# Revit family: MECON Turbo-Lux® 3 Digital
name_source: partatom
category: Rohrzubehör
units: mm (PartAtom-declared; Revit-internal decimal feet)

## family parameters
Arbeitsebenenbasiert = Nein
Beim Laden mit Abzugskörper schneiden = Nein
Bemaßung runder Anschluss = Radius verwenden
Gemeinsam genutzt = Nein
Immer vertikal = Ja
OmniClass-Nummer = 23.60.10.17
OmniClass-Titel = Flow Meters
Teiletyp = Ventil - Zerlegung in

## types (57) — shared parameters
Approval = FM
Black = Metal - black
Blue = Metal - RAL5015
Delivery Time = in stock
Download Test Certificate = https://download.mecon.de
FM Certificate = https://www.mecon.de
Glass = Glass-
Grey = Metal - grey
Hersteller = MECON GmbH, Röntgenstraße 105, 50169 Kerpen, Germany
IfcExportAs = IfcFlowMeter
IfcExportType = FLOWMETER
Operating Manual = https://www.mecon.de
Technical Data Sheet = https://www.mecon.de
URL = https://www.mecon.de
Website Product = https://www.mecon.de
iFM = Ja
iLPCB = Nein
iVdS = Nein
zero-valued in all types: Vorgabe-Ansicht

## per-type parameters (varying)
| type | Build in Length | Color_Body | Flow Range | Modell | Nominal_Diameter | Nominal_Radius | Order Code | Typenkommentare | iD2 | iR1 |
| 12"/ DN 300, 5000 USgpm (ø 323,9 mm) - stainless steel | 200 mm  [stored 0.656168 ft] | Metal - stainless steel | 2000 - 10000 USgpm / 7600 - 38000 lpm | 12"/ DN 300 for pump 5000 USgpm (ø 323,9 mm) with FM approval | 300 mm | 150 mm | TL3P0-NWS / TL3D0 | 12"/ DN 300, 5000 USgpm (ø 323,9 mm) FM - stainless steel | 240 mm  [stored 0.787402 ft] | 154 mm  [stored 0.505249 ft] |
| 12"/ DN 300, 5000 USgpm (ø 323,9 mm) - red | 200 mm  [stored 0.656168 ft] | Metal - RAL3000 | 2000 - 10000 USgpm / 7600 - 38000 lpm | 12"/ DN 300 for pump 5000 USgpm (ø 323,9 mm) with FM approval | 300 mm | 150 mm | TL3P0-NWR / TL3D0 | 12"/ DN 300, 5000 USgpm (ø 323,9 mm) FM - red | 240 mm  [stored 0.787402 ft] | 154 mm  [stored 0.505249 ft] |
| 12"/ DN 300, 5000 USgpm (ø 323,9 mm) | 200 mm  [stored 0.656168 ft] | Metal - RAL5015 | 2000 - 10000 USgpm / 7600 - 38000 lpm | 12"/ DN 300 for pump 5000 USgpm (ø 323,9 mm) with FM approval | 300 mm | 150 mm | TL3P0-NW / TL3D0 | 12"/ DN 300, 5000 USgpm (ø 323,9 mm)  FM | 240 mm  [stored 0.787402 ft] | 154 mm  [stored 0.505249 ft] |
| 10"/ DN 250, 4500 USgpm (ø 273,0 mm) - stainless steel | 200 mm  [stored 0.656168 ft] | Metal - stainless steel | 1800 - 9000 USgpm / 6800 - 34000 lpm | 10"/ DN 250 for pump 4500 USgpm (ø 273,0 mm) with FM approval | 250 mm | 125 mm | TL3P0-MVS / TL3D0 | 10"/ DN 250, 4500 USgpm (ø 273,0 mm) FM - stainless steel | 215 mm  [stored 0.705381 ft] | 129 mm |
| 10"/ DN 250, 4500 USgpm (ø 273,0 mm) - red | 200 mm  [stored 0.656168 ft] | Metal - RAL3000 | 1800 - 9000 USgpm / 6800 - 34000 lpm | 10"/ DN 250 for pump 4500 USgpm (ø 273,0 mm) with FM approval | 250 mm | 125 mm | TL3P0-MVR / TL3D0 | 10"/ DN 250, 4500 USgpm (ø 273,0 mm) FM - red | 215 mm  [stored 0.705381 ft] | 129 mm |
| 10"/ DN 250, 4500 USgpm (ø 273,0 mm) | 200 mm  [stored 0.656168 ft] | Metal - RAL5015 | 1800 - 9000 USgpm / 6800 - 34000 lpm | 10"/ DN 250 for pump 4500 USgpm (ø 273,0 mm) with FM approval | 250 mm | 125 mm | TL3P0-MV / TL3D0 | 10"/ DN 250, 4500 USgpm (ø 273,0 mm)  FM | 215 mm  [stored 0.705381 ft] | 129 mm |
| 10"/ DN 250, 4000 USgpm (ø 273,0 mm) - stainless steel | 200 mm  [stored 0.656168 ft] | Metal - stainless steel | 1600 - 8000 USgpm / 6000 - 30000 lpm | 10"/ DN 250 for pump 4000 USgpm (ø 273,0 mm) with FM approval | 250 mm | 125 mm | TL3P0-MUS / TL3D0 | 10"/ DN 250, 4000 USgpm (ø 273,0 mm) FM - stainless steel | 215 mm  [stored 0.705381 ft] | 129 mm |
| 10"/ DN 250, 4000 USgpm (ø 273,0 mm) - red | 200 mm  [stored 0.656168 ft] | Metal - RAL3000 | 1600 - 8000 USgpm / 6000 - 30000 lpm | 10"/ DN 250 for pump 4000 USgpm (ø 273,0 mm) with FM approval | 250 mm | 125 mm | TL3P0-MUR / TL3D0 | 10"/ DN 250, 4000 USgpm (ø 273,0 mm) FM - red | 215 mm  [stored 0.705381 ft] | 129 mm |
| 10"/ DN 250, 4000 USgpm (ø 273,0 mm) | 200 mm  [stored 0.656168 ft] | Metal - RAL5015 | 1600 - 8000 USgpm / 6000 - 30000 lpm | 10"/ DN 250 for pump 4000 USgpm (ø 273,0 mm) with FM approval | 250 mm | 125 mm | TL3P0-MU / TL3D0 | 10"/ DN 250, 4000 USgpm (ø 273,0 mm)  FM | 215 mm  [stored 0.705381 ft] | 129 mm |
| 10"/ DN 250, 3500 USgpm (ø 273,0 mm) - stainless steel | 200 mm  [stored 0.656168 ft] | Metal - stainless steel | 1400 - 7000 USgpm / 5300 - 26500 lpm | 10"/ DN 250 for pump 3500 USgpm (ø 273,0 mm) with FM approval | 250 mm | 125 mm | TL3P0-MTS / TL3D0 | 10"/ DN 250, 3500 USgpm (ø 273,0 mm) - stainless steel | 215 mm  [stored 0.705381 ft] | 129 mm |
| 10"/ DN 250, 3500 USgpm (ø 273,0 mm) - red | 200 mm  [stored 0.656168 ft] | Metal - RAL3000 | 1400 - 7000 USgpm / 5300 - 26500 lpm | 10"/ DN 250 for pump 3500 USgpm (ø 273,0 mm) with FM approval | 250 mm | 125 mm | TL3P0-MTR / TL3D0 | 10"/ DN 250, 3500 USgpm (ø 273,0 mm) FM - red | 215 mm  [stored 0.705381 ft] | 129 mm |
| 10"/ DN 250, 3500 USgpm (ø 273,0 mm) | 200 mm  [stored 0.656168 ft] | Metal - RAL5015 | 1400 - 7000 USgpm / 5300 - 26500 lpm | 10"/ DN 250 for pump 3500 USgpm (ø 273,0 mm) with FM approval | 250 mm | 125 mm | TL3P0-MT / TL3D0 | 10"/ DN 250, 3500 USgpm (ø 273,0 mm) FM | 215 mm  [stored 0.705381 ft] | 129 mm |
| 8"/ DN 200, 3000 USgpm (ø 219,1 mm) - stainless steel | 200 mm  [stored 0.656168 ft] | Metal - stainless steel | 1200 - 6000 USgpm / 4500 - 22500 lpm | 8"/ DN 200 for pump 3000 USgpm (ø 219,1 mm) with FM approval | 200 mm | 100 mm | TL3P0-LSS / TL3D0 | 8"/ DN 200, 3000 USgpm (ø 219,1 mm) FM - stainless steel | 190 mm  [stored 0.62336 ft] | 104 mm |
| 8"/ DN 200, 3000 USgpm (ø 219,1 mm) - red | 200 mm  [stored 0.656168 ft] | Metal - RAL3000 | 1200 - 6000 USgpm / 4500 - 22500 lpm | 8"/ DN 200 for pump 3000 USgpm (ø 219,1 mm) with FM approval | 200 mm | 100 mm | TL3P0-LSR / TL3D0 | 8"/ DN 200, 3000 USgpm (ø 219,1 mm) FM - red | 190 mm  [stored 0.62336 ft] | 104 mm |
| 8"/ DN 200, 3000 USgpm (ø 219,1 mm) | 200 mm  [stored 0.656168 ft] | Metal - RAL5015 | 1200 - 6000 USgpm / 4500 - 22 500 lpm | 8"/ DN 200 for pump 3000 USgpm (ø 219,1 mm) with FM approval | 200 mm | 100 mm | TL3P0-LS / TL3D0 | 8"/ DN 200, 3000 USgpm (ø 219,1 mm) FM | 190 mm  [stored 0.62336 ft] | 104 mm |
| 8"/ DN 200, 2500 USgpm (ø 219,1 mm) - stainless steel | 200 mm  [stored 0.656168 ft] | Metal - stainless steel | 1000 - 5000 USgpm / 3800 - 19000 lpm | 8"/ DN 200 for pump 2500 USgpm (ø 219,1 mm) with FM approval | 200 mm | 100 mm | TL3P0-LRS / TL3D0 | 8"/ DN 200, 2500 USgpm (ø 219,1 mm) FM - stainless steel | 190 mm  [stored 0.62336 ft] | 104 mm |
| 8"/ DN 200, 2500 USgpm (ø 219,1 mm) - red | 200 mm  [stored 0.656168 ft] | Metal - RAL3000 | 1000 - 5000 USgpm / 3800 - 19000 lpm | 8"/ DN 200 for pump 2500 USgpm (ø 219,1 mm) with FM approval | 200 mm | 100 mm | TL3P0-LRR / TL3D0 | 8"/ DN 200, 2500 USgpm (ø 219,1 mm) FM - red | 190 mm  [stored 0.62336 ft] | 104 mm |
| 8"/ DN 200, 2500 USgpm (ø 219,1 mm) | 200 mm  [stored 0.656168 ft] | Metal - RAL5015 | 1000 - 5000 USgpm / 3800 - 19000 lpm | 8"/ DN 200 for pump 2500 USgpm (ø 219,1 mm) with FM approval | 200 mm | 100 mm | TL3P0-LR / TL3D0 | 8"/ DN 200, 2500 USgpm (ø 219,1 mm) FM | 190 mm  [stored 0.62336 ft] | 104 mm |
| 8"/ DN 200, 2000 USgpm (ø 219,1 mm) - stainless steel | 200 mm  [stored 0.656168 ft] | Metal - stainless steel | 800 - 4000 USgpm / 3000 - 15000 lpm | 8"/ DN 200 for pump 2000 USgpm (ø 219,1 mm) with FM approval | 200 mm | 100 mm | TL3P0-LQS / TL3D0 | 8"/ DN 200, 2000 USgpm (ø 219,1 mm) FM - stainless steel | 190 mm  [stored 0.62336 ft] | 104 mm |
| 8"/ DN 200, 2000 USgpm (ø 219,1 mm) - red | 200 mm  [stored 0.656168 ft] | Metal - RAL3000 | 800 - 4000 USgpm / 3000 - 15000 lpm | 8"/ DN 200 for pump 2000 USgpm (ø 219,1 mm) with FM approval | 200 mm | 100 mm | TL3P0-LQR / TL3D0 | 8"/ DN 200, 2000 USgpm (ø 219,1 mm) FM - red | 190 mm  [stored 0.62336 ft] | 104 mm |
| 8"/ DN 200, 2000 USgpm (ø 219,1 mm) | 200 mm  [stored 0.656168 ft] | Metal - RAL5015 | 800 - 4000 USgpm / 3000 - 15000 lpm | 8"/ DN 200 for pump 2000 USgpm (ø 219,1 mm) with FM approval | 200 mm | 100 mm | TL3P0-LQ / TL3D0 | 8"/ DN 200, 2000 USgpm (ø 219,1 mm) FM | 190 mm  [stored 0.62336 ft] | 104 mm |
| 8"/ DN 200, 1500 USgpm (ø 219,1 mm) - stainless steel | 200 mm  [stored 0.656168 ft] | Metal - stainless steel | 600 - 3000 USgpm / 2200 - 11000 lpm | 8"/ DN 200 for pump 1500 USgpm (ø 219,1 mm) with FM approval | 200 mm | 100 mm | TL3P0-LPS / TL3D0 | 8"/ DN 200, 1500 USgpm (ø 219,1 mm) FM - stainless steel | 190 mm  [stored 0.62336 ft] | 104 mm |
| 8"/ DN 200, 1500 USgpm (ø 219,1 mm) - red | 200 mm  [stored 0.656168 ft] | Metal - RAL3000 | 600 - 3000 USgpm / 2200 - 11000 lpm | 8"/ DN 200 for pump 1500 USgpm (ø 219,1 mm) with FM approval | 200 mm | 100 mm | TL3P0-LPR / TL3D0 | 8"/ DN 200, 1500 USgpm (ø 219,1 mm) FM - red | 190 mm  [stored 0.62336 ft] | 104 mm |
| 8"/ DN 200, 1500 USgpm (ø 219,1 mm) | 200 mm  [stored 0.656168 ft] | Metal - RAL5015 | 600 - 3000 USgpm / 2200 - 11000 lpm | 8"/ DN 200 for pump 1500 USgpm (ø 219,1 mm) with FM approval | 200 mm | 100 mm | TL3P0-LP / TL3D0 | 8"/ DN 200, 1500 USgpm (ø 219,1 mm) FM | 190 mm  [stored 0.62336 ft] | 104 mm |
| 6"/ DN 150, 1250 USgpm (ø 165,1 mm) - stainless steel | 200 mm  [stored 0.656168 ft] | Metal - stainless steel | 500 - 2500 USgpm / 1900 - 9500 lpm | 6"/ DN 150 for pump 1250 USgpm (ø 165,1 mm) with FM approval | 150 mm | 75 mm | TL3P0-XNS / TL3D0 | 6"/ DN 150, 1250 USgpm (ø 165,1 mm) FM - stainless steel | 165 mm  [stored 0.541339 ft] | 79 mm |
| 6"/ DN 150, 1250 USgpm (ø 165,1 mm) - red | 200 mm  [stored 0.656168 ft] | Metal - RAL3000 | 500 - 2500 USgpm / 1900 - 9500 lpm | 6"/ DN 150 for pump 1250 USgpm (ø 165,1 mm) with FM approval | 150 mm | 75 mm | TL3P0-XNR / TL3D0 | 6"/ DN 150, 1250 USgpm (ø 165,1 mm) FM - red | 165 mm  [stored 0.541339 ft] | 79 mm |
| 6"/ DN 150, 1250 USgpm (ø 165,1 mm) | 200 mm  [stored 0.656168 ft] | Metal - RAL5015 | 500 - 2500 USgpm / 1900 - 9500 lpm | 6"/ DN 150 for pump 1250 USgpm (ø 165,1 mm) with FM approval | 150 mm | 75 mm | TL3P0-XN / TL3D0 | 6"/ DN 150, 1250 USgpm (ø 165,1 mm) FM | 165 mm  [stored 0.541339 ft] | 79 mm |
| 6"/ DN 150, 1000 USgpm (ø 165,1 mm) - stainless steel | 200 mm  [stored 0.656168 ft] | Metal - stainless steel | 400 - 2000 USgpm / 1500 - 7500 lpm | 6"/ DN 150 for pump 1000 USgpm (ø 165,1 mm) with FM approval | 150 mm | 75 mm | TL3P0-XMS / TL3D0 | 6"/ DN 150, 1000 USgpm (ø 165,1 mm) FM - stainless steel | 165 mm  [stored 0.541339 ft] | 79 mm |
| 6"/ DN 150, 1000 USgpm (ø 165,1 mm) - red | 200 mm  [stored 0.656168 ft] | Metal - RAL3000 | 400 - 2000 USgpm / 1500 - 7500 lpm | 6"/ DN 150 for pump 1000 USgpm (ø 165,1 mm) with FM approval | 150 mm | 75 mm | TL3P0-XMR / TL3D0 | 6"/ DN 150, 1000 USgpm (ø 165,1 mm) FM - red | 165 mm  [stored 0.541339 ft] | 79 mm |
| 6"/ DN 150, 1000 USgpm (ø 165,1 mm) | 200 mm  [stored 0.656168 ft] | Metal - RAL5015 | 400 - 2000 USgpm / 1500 - 7500 lpm | 6"/ DN 150 for pump 1000 USgpm (ø 165,1 mm) with FM approval | 150 mm | 75 mm | TL3P0-XM / TL3D0 | 6"/ DN 150, 1000 USgpm (ø 165,1 mm) FM | 165 mm  [stored 0.541339 ft] | 79 mm |
| 6"/ DN 150, 750 USgpm (ø 165,1 mm) - stainless steel | 200 mm  [stored 0.656168 ft] | Metal - stainless steel | 300 - 1500 USgpm / 1130 - 5650 lpm | 6"/ DN 150 for pump 750 USgpm (ø 165,1 mm) with FM approval | 150 mm | 75 mm | TL3P0-XLS / TL3D0 | 6"/ DN 150, 750 USgpm (ø 165,1 mm) FM - stainless steel | 165 mm  [stored 0.541339 ft] | 79 mm |
| 6"/ DN 150, 750 USgpm (ø 165,1 mm) - red | 200 mm  [stored 0.656168 ft] | Metal - RAL3000 | 300 - 1500 USgpm / 1130 - 5650 lpm | 6"/ DN 150 for pump 750 USgpm (ø 165,1 mm) with FM approval | 150 mm | 75 mm | TL3P0-XLR / TL3D0 | 6"/ DN 150, 750 USgpm (ø 165,1 mm) FM - red | 165 mm  [stored 0.541339 ft] | 79 mm |
| 6"/ DN 150, 750 USgpm (ø 165,1 mm) | 200 mm  [stored 0.656168 ft] | Metal - RAL5015 | 300 - 1500 USgpm / 1130 - 5650 lpm | 6"/ DN 150 for pump 750 USgpm (ø 165,1 mm) with FM approval | 150 mm | 75 mm | TL3P0-XL / TL3D0 | 6"/ DN 150, 750 USgpm (ø 165,1 mm) FM | 165 mm  [stored 0.541339 ft] | 79 mm |
| 6"/ DN 150, 500 USgpm (ø 165,1 mm) - stainless steel | 200 mm  [stored 0.656168 ft] | Metal - stainless steel | 200 - 1000 USgpm / 760 - 3800 lpm | 6"/ DN 150 for pump 500 USgpm (ø 165,1 mm) with FM approval | 150 mm | 75 mm | TL3P0-XKS / TL3D0 | 6"/ DN 150, 500 USgpm (ø 165,1 mm) FM - stainless steel | 165 mm  [stored 0.541339 ft] | 79 mm |
| 6"/ DN 150, 500 USgpm (ø 165,1 mm) - red | 200 mm  [stored 0.656168 ft] | Metal - RAL3000 | 200 - 1000 USgpm / 760 - 3800 lpm | 6"/ DN 150 for pump 500 USgpm (ø 165,1 mm) with FM approval | 150 mm | 75 mm | TL3P0-XKR / TL3D0 | 6"/ DN 150, 500 USgpm (ø 165,1 mm) FM - red | 165 mm  [stored 0.541339 ft] | 79 mm |
| 6"/ DN 150, 500 USgpm (ø 165,1 mm) | 200 mm  [stored 0.656168 ft] | Metal - RAL5015 | 200 - 1000 USgpm / 760 - 3800 lpm | 6"/ DN 150 for pump 500 USgpm (ø 165,1 mm) with FM approval | 150 mm | 75 mm | TL3P0-XK / TL3D0 | 6"/ DN 150, 500 USgpm (ø 165,1 mm) FM | 165 mm  [stored 0.541339 ft] | 79 mm |
| 6"/ DN 150, 1250 USgpm (ø 168,3 mm) - stainless steel | 200 mm  [stored 0.656168 ft] | Metal - stainless steel | 500 - 2500 USgpm / 1900 - 9500 lpm | 6"/ DN 150 for pump 1250 USgpm (ø 168,3 mm) with FM approval | 150 mm | 75 mm | TL3P0-KNS / TL3D0 | 6"/ DN 150, 1250 USgpm (ø 168,3 mm) FM - stainless steel | 165 mm  [stored 0.541339 ft] | 79 mm |
| 6"/ DN 150, 1250 USgpm (ø 168,3 mm) - red | 200 mm  [stored 0.656168 ft] | Metal - RAL3000 | 500 - 2500 USgpm / 1900 - 9500 lpm | 6"/ DN 150 for pump 1250 USgpm (ø 168,3 mm) with FM approval | 150 mm | 75 mm | TL3P0-KNR / TL3D0 | 6"/ DN 150, 1250 USgpm (ø 168,3 mm) FM - red | 165 mm  [stored 0.541339 ft] | 79 mm |
| 6"/ DN 150, 1250 USgpm (ø 168,3 mm) | 200 mm  [stored 0.656168 ft] | Metal - RAL5015 | 500 - 2500 USgpm / 1900 - 9500 lpm | 6"/ DN 150 for pump 1250 USgpm (ø 168,3 mm) with FM approval | 150 mm | 75 mm | TL3P0-KN / TL3D0 | 6"/ DN 150, 1250 USgpm (ø 168,3 mm) FM | 165 mm  [stored 0.541339 ft] | 79 mm |
| 6"/ DN 150, 1000 USgpm (ø 168,3 mm) - stainless steel | 200 mm  [stored 0.656168 ft] | Metal - stainless steel | 400 - 2000 USgpm / 1500 - 7500 lpm | 6"/ DN 150 for pump 1000 USgpm (ø 168,3 mm) with FM approval | 150 mm | 75 mm | TL3P0-KMS / TL3D0 | 6"/ DN 150, 1000 USgpm (ø 168,3 mm) FM - stainless steel | 165 mm  [stored 0.541339 ft] | 79 mm |
| 6"/ DN 150, 1000 USgpm (ø 168,3 mm) - red | 200 mm  [stored 0.656168 ft] | Metal - RAL3000 | 400 - 2000 USgpm / 1500 - 7500 lpm | 6"/ DN 150 for pump 1000 USgpm (ø 168,3 mm) with FM approval | 150 mm | 75 mm | TL3P0-KMR / TL3D0 | 6"/ DN 150, 1000 USgpm (ø 168,3 mm) FM - red | 165 mm  [stored 0.541339 ft] | 79 mm |
| 6"/ DN 150, 1000 USgpm (ø 168,3 mm) | 200 mm  [stored 0.656168 ft] | Metal - RAL5015 | 400 - 2000 USgpm / 1500 - 7500 lpm | 6"/ DN 150 for pump 1000 USgpm (ø 168,3 mm) with FM approval | 150 mm | 75 mm | TL3P0-KM / TL3D0 | 6"/ DN 150, 1000 USgpm (ø 168,3 mm) FM | 165 mm  [stored 0.541339 ft] | 79 mm |
| 6"/ DN 150, 750 USgpm (ø 168,3 mm) - stainless steel | 200 mm  [stored 0.656168 ft] | Metal - stainless steel | 300 -1500 USgpm / 1130 - 5650 lpm | 6"/ DN 150 for pump 750 USgpm (ø 168,3 mm) with FM approval | 150 mm | 75 mm | TL3P0-KLS / TL3D0 | 6"/ DN 150, 750 USgpm (ø 168,3 mm) FM - stainless steel | 165 mm  [stored 0.541339 ft] | 79 mm |
| 6"/ DN 150, 750 USgpm (ø 168,3 mm) - red | 200 mm  [stored 0.656168 ft] | Metal - RAL3000 | 300 -1500 USgpm / 1130 - 5650 lpm | 6"/ DN 150 for pump 750 USgpm (ø 168,3 mm) with FM approval | 150 mm | 75 mm | TL3P0-KLR / TL3D0 | 6"/ DN 150, 750 USgpm (ø 168,3 mm) FM - red | 165 mm  [stored 0.541339 ft] | 79 mm |
| 6"/ DN 150, 750 USgpm (ø 168,3 mm) | 200 mm  [stored 0.656168 ft] | Metal - RAL5015 | 300 -1500 USgpm / 1130 - 5650 lpm | 6"/ DN 150 for pump 750 USgpm (ø 168,3 mm) with FM approval | 150 mm | 75 mm | TL3P0-KL / TL3D0 | 6"/ DN 150, 750 USgpm (ø 168,3 mm) FM | 165 mm  [stored 0.541339 ft] | 79 mm |
| 6"/ DN 150, 500 USgpm (ø 168,3 mm) - stainless steel | 200 mm  [stored 0.656168 ft] | Metal - stainless steel | 200 - 1000 USgpm / 760 - 3800 lpm | 4"/ DN 100 for pump 250 USgpm (ø 114,3 mm) with FM approval | 150 mm | 75 mm | TL3P0-KKS / TL3D0 | 6"/ DN 150, 500 USgpm (ø 168,3 mm) FM - stainless steel | 165 mm  [stored 0.541339 ft] | 79 mm |
| 6"/ DN 150, 500 USgpm (ø 168,3 mm) - red | 200 mm  [stored 0.656168 ft] | Metal - RAL3000 | 200 - 1000 USgpm / 760 - 3800 lpm | 6"/ DN 150 for pump 500 USgpm (ø 168,3 mm) with FM approval | 150 mm | 75 mm | TL3P0-KKR / TL3D0 | 6"/ DN 150, 500 USgpm (ø 168,3 mm) FM - red | 165 mm  [stored 0.541339 ft] | 79 mm |
| 6"/ DN 150, 500 USgpm (ø 168,3 mm) | 200 mm  [stored 0.656168 ft] | Metal - RAL5015 | 200 - 1000 USgpm / 760 - 3800 lpm | 6"/ DN 150 for pump 500 USgpm (ø 168,3 mm) with FM approval | 150 mm | 75 mm | TL3P0-KK / TL3D0 | 6"/ DN 150, 500 USgpm (ø 168,3 mm) FM | 165 mm  [stored 0.541339 ft] | 79 mm |
| 4"/ DN 100, 450 USgpm (ø 114,3 mm) | 100 mm  [stored 0.328084 ft] | Metal - RAL5015 | 180 - 900 USgpm / 680 - 3400 lpm | 4"/ DN 100 for pump 450 USgpm (ø 114,3 mm) with FM approval | 100 mm | 50 mm | TL3P0-HJ / TL3D0 | 4"/ DN 100, 450 USgpm (ø 114,3 mm) FM | 140 mm  [stored 0.459318 ft] | 54 mm |
| 4"/ DN 100, 400 USgpm (ø 114,3 mm) | 100 mm  [stored 0.328084 ft] | Metal - RAL5015 | 160 - 800 USgpm / 600 - 3000 lpm | 4"/ DN 100 for pump 400 USgpm (ø 114,3 mm) with FM approval | 100 mm | 50 mm | TL3P0-HH / TL3D0 | 4"/ DN 100, 400 USgpm (ø 114,3 mm) FM | 140 mm  [stored 0.459318 ft] | 54 mm |
| 4"/ DN 100, 300 USgpm (ø 114,3 mm) | 100 mm  [stored 0.328084 ft] | Metal - RAL5015 | 120 - 600 USgpm / 460 - 2300 lpm | 4"/ DN 100 for pump 300 USgpm (ø 114,3 mm) with FM approval | 100 mm | 50 mm | TL3P0-HG / TL3D0 | 4"/ DN 100, 300 USgpm (ø 114,3 mm) FM | 140 mm  [stored 0.459318 ft] | 54 mm |
| 4"/ DN 100, 250 USgpm (ø 114,3 mm) | 100 mm  [stored 0.328084 ft] | Metal - RAL5015 | 100 - 500 USgpm / 380 - 1900 lpm | 4"/ DN 100 for pump 250 USgpm (ø 114,3 mm) with FM approval | 100 mm | 50 mm | TL3P0-HF / TL3D0 | 4"/ DN 100, 250 USgpm (ø 114,3 mm) FM | 140 mm  [stored 0.459318 ft] | 54 mm |
| 3"/ DN 80, 200 USgpm (ø 88,9 mm) | 100 mm  [stored 0.328084 ft] | Metal - RAL5015 | 80 - 400 USgpm / 300 - 1500 lpm | 3"/ DN 80 for pump 200 USgpm (ø 88,9 mm) with FM approval | 80 mm | 40 mm | TL3P0-GE / TL3D0 | 3"/ DN 80, 200 USgpm (ø 88,9 mm) FM | 130 mm | 44 mm |
| 3"/ DN 80, 150 USgpm (ø 88,9 mm) | 100 mm  [stored 0.328084 ft] | Metal - RAL5015 | 60 - 300 USgpm / 220 - 1100 lpm | 3"/ DN 80 for pump 150 USgpm (ø 88,9 mm) with FM approval | 80 mm | 40 mm | TL3P0-GD / TL3D0 | 3"/ DN 80, 150 USgpm (ø 88,9 mm) FM | 130 mm | 44 mm |
| 2½"/ DN 65, 100 USgpm (ø 76,1 mm) | 100 mm  [stored 0.328084 ft] | Metal - RAL5015 | 40 - 200 USgpm / 150 - 750 lpm | 2½"/ DN 65 for pump 100 USgpm (ø 76,1 mm) with FM approval | 65 mm | 33 mm | TL3P0-FC / TL3D0 | 2½"/ DN 65, 100 USgpm (ø 76,1 mm) FM | 122.5 mm | 36.5 mm |
| 2½"/ DN 65, 100 USgpm (ø 73,0 mm) | 100 mm  [stored 0.328084 ft] | Metal - RAL5015 | 40 - 200 USgpm / 150 - 750 lpm | 2½"/ DN 65 for pump 100 USgpm (ø 73,0 mm) with FM approval | 65 mm | 33 mm | TL3P0-UC / TL3D0 | 2½"/ DN 65, 100 USgpm (ø 73,0 mm) FM | 122.5 mm | 36.5 mm |
| 2"/ DN 50, 50 USgpm (ø 60,3 mm) | 100 mm  [stored 0.328084 ft] | Metal - RAL5015 | 20 - 100 USgpm / 75 - 375 lpm | 2"/ DN 50 for pump 50 USgpm (ø 60,3 mm) with FM approval | 50 mm | 25 mm | TL3P0-EB / TL3D0 | 2"/ DN 50, 50 USgpm (ø 60,3 mm) FM | 115 mm | 29 mm |

note: [stored X ft] marks values corroborated as IEEE doubles in the binary element streams (Revit-internal decimal feet)
